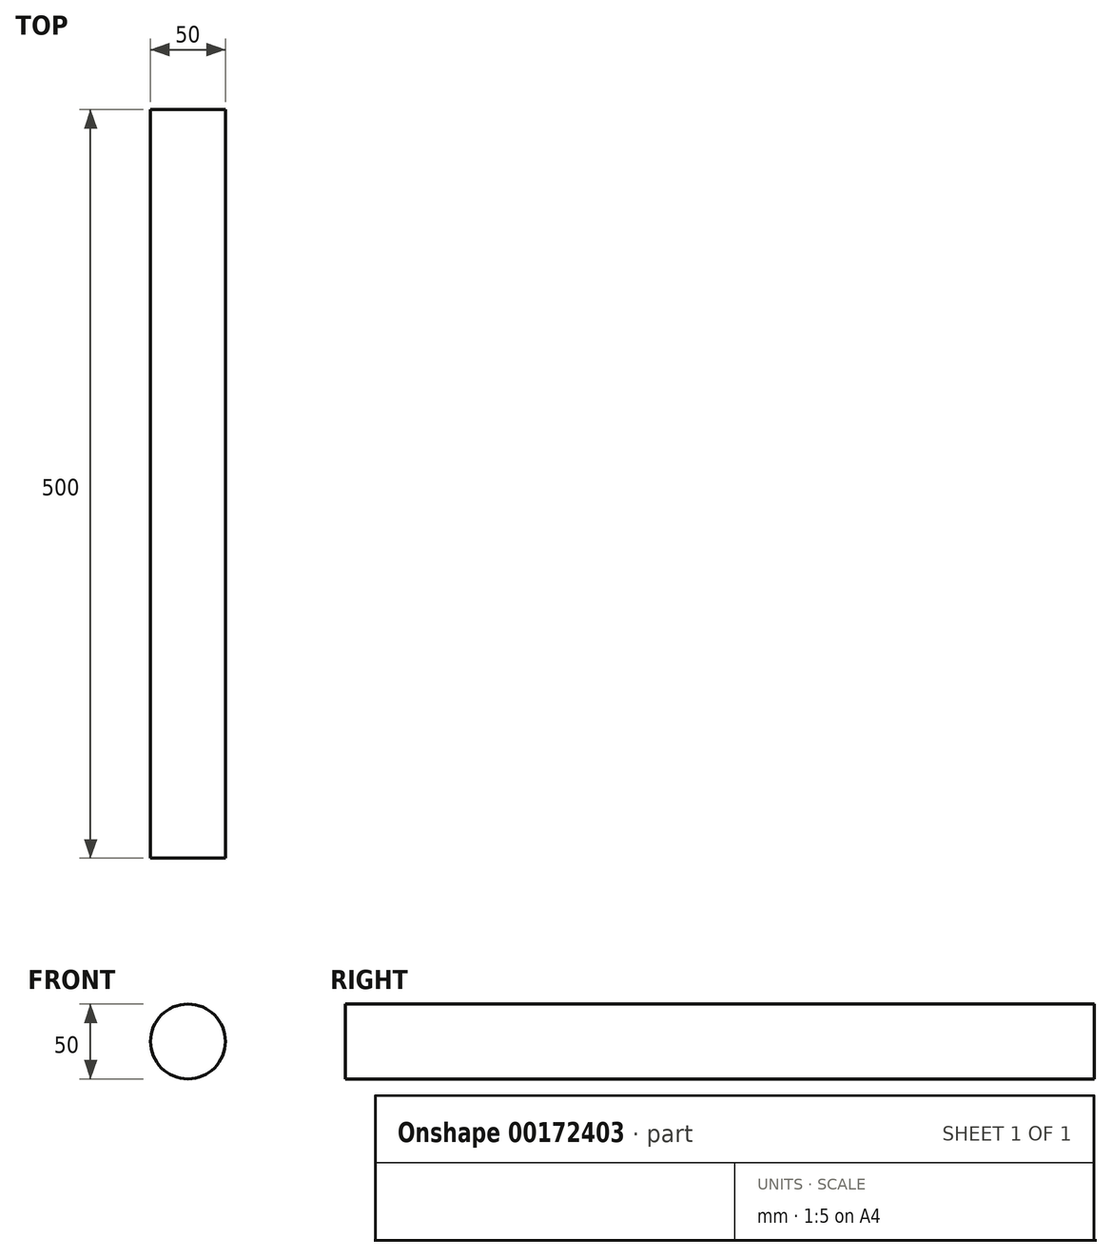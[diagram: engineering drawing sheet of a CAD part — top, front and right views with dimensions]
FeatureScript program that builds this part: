
annotation { "Feature Type Name" : "Feature", "Feature Type Description" : "" }
export const myFeature = defineFeature(function(context is Context, id is Id, definition is map)
    precondition{}
    {
        {
            var Q0;
            Q0=qCreatedBy(makeId("Front.planeOp"),FACE);
            var sketch = newSketch(context, id + "F0", { "sketchPlane" : qUnion([Q0])});
            skCircle(sketch, "E0", {"center": v(0, 0) * mm, "radius": 25 * mm});
            skSolve(sketch);
        }
        {
            var Q0;
            Q0 = qSketchRegion(id + "F0", true);
            extrude(context, id + "F1", {"entities" : qUnion([Q0]), "depth" : 500 * mm});
        }
    });
